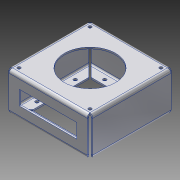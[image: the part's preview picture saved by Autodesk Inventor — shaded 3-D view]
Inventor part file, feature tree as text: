
AUTODESK INVENTOR PART (.ipt)
format: ipt  version: 2015 (Build 190159000, 159)  size: 444,416 bytes
history: native  units: in
note: dims shown in document units (in); Inventor stores cm internally (conversion verified against a paired STEP export)
features: sheet_metal_op x7, other x7, sketch x5, projected_geometry x4, hole x2
ambient origin geometry x8: Origin, YZ Plane, XZ Plane, XY Plane, X Axis, Y Axis, Z Axis, Center Point
bodies: Solid1 (feature_tree)
feature tree (25):
  sketch  "Sketch1"  dims[d4=0.133in d5=0.133in]
  sheet_metal_op  "Face1"
  hole  "Hole1"  [1 undecoded]
  sheet_metal_op  "Flange2"
  sheet_metal_op  "Flange3"
  other  "A-Side Definition"
  hole  "Hole2"  [1 undecoded]
  other  "Plate1"
  sketch  "Sketch3"  dims[d6=0.047in d7=0.047in]
  other  "Plate3"
  sheet_metal_op  "Bend2"
  sheet_metal_op  "Corner2"
  sketch  "Sketch4"  dims[d8=0.133in]
  other  "Plate4"
  sheet_metal_op  "Bend3"
  sheet_metal_op  "Corner3"
  sketch  "Sketch7"  dims[d9=0.047in]
  projected_geometry  "Projected Loop5"
  projected_geometry  "Projected Loop6"
  projected_geometry  "Projected Loop7"
  projected_geometry  "Projected Loop8"
  sketch  "Sketch8"  dims[d10=2.34in d11=2.34in d12=0.047in d13=0.133in d14=0.047in d15=0.133in d16=6.063in d17=6.063in d18=0.117in d19=0.25in d20=0.25in d21=0.25in d22=0.578in d23=0.25in d24=0.625in d25=0.625in d26=5.68in d27=0.25in d28=5.813in d29=5.813in d30=5.766in d31=0.625in d32=5.813in d33=5.813in d34=0.6915in d35=3.0315in d36=3.0315in d37=3.0315in d38=0.203in d39=5.438in d40=0.25in d41=0.25in d42=0.117in d43=5.813in d44=0.25in d45=0.25in d46=5.391in d47=5.813in d48=5.438in d49=5.438in d50=5.68in d51=5.813in d52=5.813in d53=5.813in d54=4.0in d55=0.125in d56=0.125in d57=0.0in d58=0.25in d59=0.75in d60=0.375in d61=0.25in d62=0.5635in d63=0.125in d64=0.8108in d75=0.125in d76=0.0625in d77=0.25in d78=0.125in d79=3.0in d80=90.0deg d81=0.125in d82=0.5in d83=0.125in d84=0.125in d85=0.3937in d86=0.125in d87=0.0625in d88=0.25in d89=0.125in d90=1.0in d91=90.0deg d92=0.125in d93=0.5in d94=0.125in d95=0.125in d96=0.75in d97=0.75in d98=0.75in d99=0.75in d100=0.25in d101=0.25in d102=0.25in d103=0.25in d104=0.25in d105=2.5681in d106=0.375in d107=0.7874in d109=1.5in d110=0.7874in d112=1.5in d115=0.7874in d117=1.5in d118=0.7874in d120=1.5in d123=0.7874in d125=1.5in d126=0.7874in d128=1.5in d131=0.7874in d133=1.5in d134=0.7874in d136=1.5in d139=0.266in d140=0.75in d141=0.507in d142=0.25in d143=0.5635in d144=0.125in d145=0.8108in d146=4.5in d147=1.125in d148=0.125in d149=0.0in]
  other  "Cut1"
  other  "Cut2"
  other  "Definition1"
note: 2 required parameter values undecoded (feature->parameter linkage not recoverable at this tier; creation-order binding heuristic only, values carry confidence <= 0.55)
